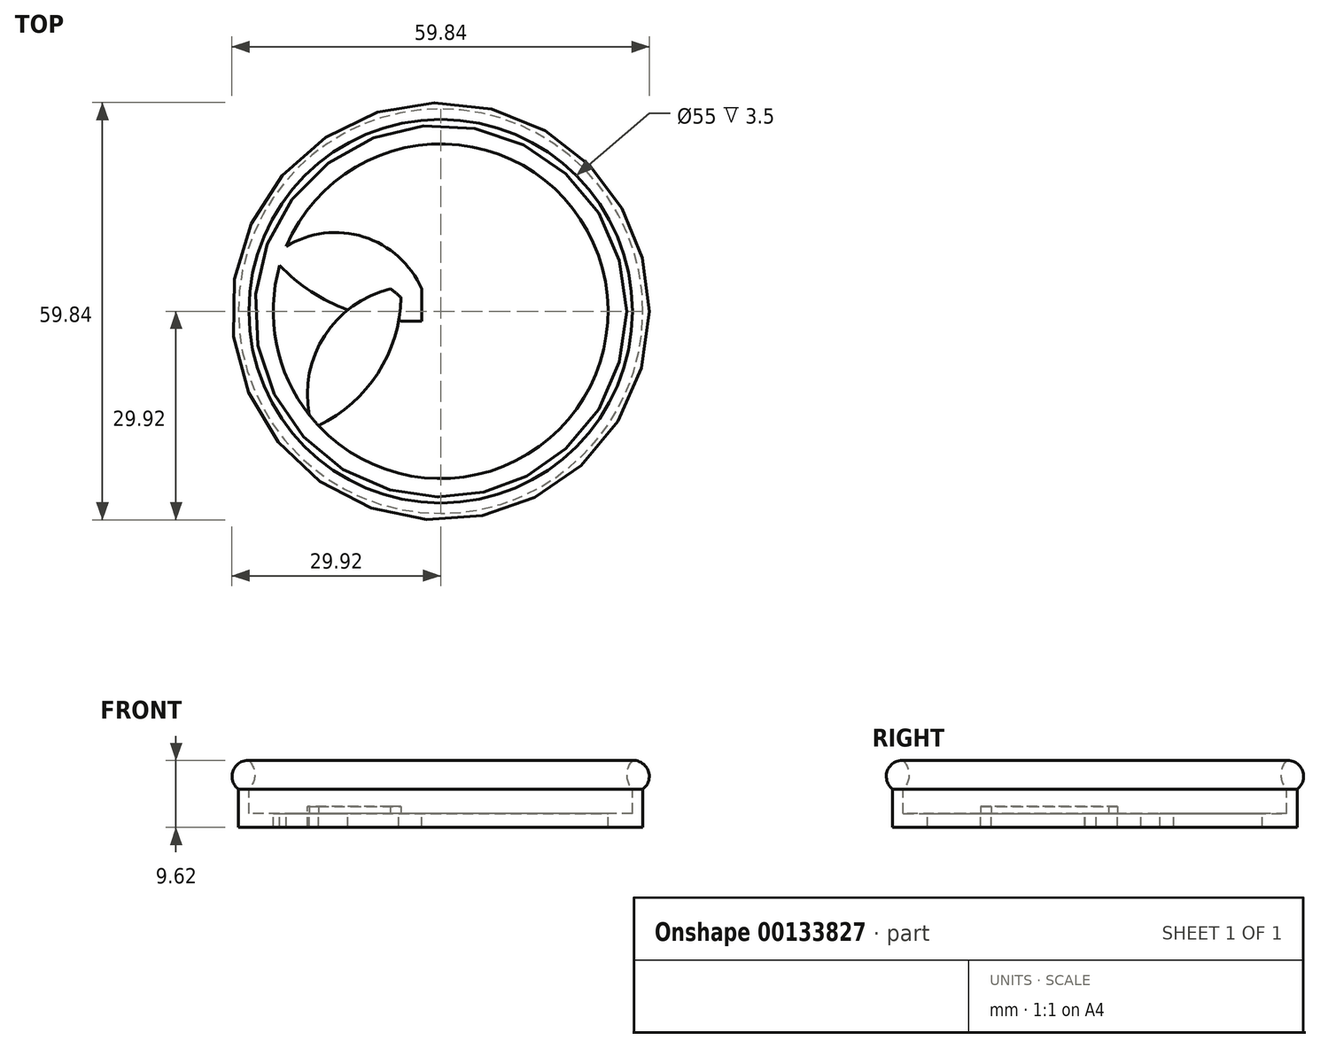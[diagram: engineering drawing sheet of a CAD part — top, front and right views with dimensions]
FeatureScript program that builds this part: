
annotation { "Feature Type Name" : "Feature", "Feature Type Description" : "" }
export const myFeature = defineFeature(function(context is Context, id is Id, definition is map)
    precondition{}
    {
        {
            var Q0;
            Q0=qCreatedBy(makeId("Front.planeOp"),FACE);
            var sketch = newSketch(context, id + "F0", { "sketchPlane" : qUnion([Q0])});
            skLineSegment(sketch, "E0", {"start": v(0, 25.71) * mm, "end": v(0, -20.29) * mm, "construction": true});
            skLineSegment(sketch, "E1", {"start": v(0, -20.29) * mm, "end": v(-42.81, -11.54) * mm, "construction": true});
            skLineSegment(sketch, "E2.0", {"start": v(-24, 25.71) * mm, "end": v(-24, -20.29) * mm, "construction": true});
            skLineSegment(sketch, "E3.0", {"start": v(-29, 25.71) * mm, "end": v(-29, -20.29) * mm, "construction": true});
            skLineSegment(sketch, "E4.0", {"start": v(-27.5, 25.71) * mm, "end": v(-27.5, -20.29) * mm, "construction": true});
            skLineSegment(sketch, "E5", {"start": v(-24, 0) * mm, "end": v(-29, 0) * mm});
            skLineSegment(sketch, "E6", {"start": v(-24, 0) * mm, "end": v(-24, 2) * mm});
            skLineSegment(sketch, "E7", {"start": v(-24, 2) * mm, "end": v(-27.5, 2) * mm});
            skLineSegment(sketch, "E8", {"start": v(-27.5, 2) * mm, "end": v(-27.5, 5.5) * mm});
            skLineSegment(sketch, "E9", {"start": v(-27.5, 5.5) * mm, "end": v(-29, 5.5) * mm});
            skLineSegment(sketch, "E10", {"start": v(-29, 5.5) * mm, "end": v(-29, 0) * mm});
            skArc(sketch, "E11", {"start": v(-27.5, 5.5) * mm, "mid": v(-26.66, 7.56) * mm, "end": v(-27.5, 9.62) * mm});
            skArc(sketch, "E12", {"start": v(-27.5, 9.62) * mm, "mid": v(-29.78, 8.11) * mm, "end": v(-29, 5.5) * mm});
            skSolve(sketch);
        }
        {
            var Q0;
            Q0=makeQuery(id+"F0.imprint","IMPRINT",FACE,{"disambiguationData":[TD([[makeQuery(id+"F0.imprint","IMPRINT",EDGE,{"derivedFrom":sQuery(id+"F0.wireOp",EDGE,"E5")}),-1.0]])]});
            var Q1;
            Q1=makeQuery(id+"F0.imprint","IMPRINT",FACE,{"disambiguationData":[TD([[makeQuery(id+"F0.imprint","IMPRINT",EDGE,{"derivedFrom":sQuery(id+"F0.wireOp",EDGE,"E9")}),-1.0]])]});
            var Q2;
            Q2=sQuery(id+"F0.wireOp",EDGE,"E0");
            revolve(context, id + "F1", {"entities" : qUnion([Q0, Q1]), "axis" : qUnion([Q2]), "revolveType" : RevolveType.FULL});
        }
        {
            var Q0;
            Q0=makeQuery(id+"F1.opRevolve","SWEPT_FACE",FACE,{"disambiguationData":[OSD([sQuery(id+"F0.wireOp",EDGE,"E7")])]});
            var sketch = newSketch(context, id + "F2", { "sketchPlane" : qUnion([Q0])});
            skCircle(sketch, "E13.0", {"center": v(0, 0) * mm, "radius": 24 * mm});
            skLineSegment(sketch, "E14", {"start": v(-2.72, 23.85) * mm, "end": v(-2.72, -23.85) * mm});
            skLineSegment(sketch, "E15", {"start": v(23.85, -2.68) * mm, "end": v(23.54, -2.01) * mm});
            skLineSegment(sketch, "E16", {"start": v(13, 20.18) * mm, "end": v(1.5, 23.95) * mm});
            skLineSegment(sketch, "E17", {"start": v(1.5, 19.86) * mm, "end": v(1.5, -17.1) * mm});
            skLineSegment(sketch, "E18", {"start": v(1.5, -17.1) * mm, "end": v(19.97, -1.22) * mm});
            skLineSegment(sketch, "E19", {"start": v(19.97, -1.22) * mm, "end": v(11.75, 17.98) * mm});
            skLineSegment(sketch, "E20", {"start": v(11.75, 17.98) * mm, "end": v(1.5, 19.86) * mm});
            skLineSegment(sketch, "E21", {"start": v(1.4, -23.96) * mm, "end": v(23.34, -5.58) * mm});
            skLineSegment(sketch, "E22", {"start": v(14.12, 19.4) * mm, "end": v(23.54, -2.01) * mm});
            skArc(sketch, "E23", {"start": v(-2.72, 3.2) * mm, "mid": v(-11.04, 10.67) * mm, "end": v(-22.13, 9.3) * mm});
            skArc(sketch, "E24", {"start": v(-2.72, -1.4) * mm, "mid": v(-11.69, 5.69) * mm, "end": v(-23.08, 6.57) * mm});
            skArc(sketch, "E25", {"start": v(-17.53, -16.4) * mm, "mid": v(-9, -8.9) * mm, "end": v(-5.67, 1.96) * mm});
            skArc(sketch, "E26", {"start": v(-7.2, 3.2) * mm, "mid": v(-16.63, -3.5) * mm, "end": v(-18.83, -14.88) * mm});
            skArc(sketch, "E27", {"start": v(-23.08, 6.57) * mm, "mid": v(-13.77, 0.36) * mm, "end": v(-2.72, -1.4) * mm});
            skSolve(sketch);
        }
        {
            var Q0;
            {var subQ0=sQuery(id+"F2.wireOp",EDGE,"E14");Q0=makeQuery(id+"F2.imprint","IMPRINT",FACE,{"disambiguationData":[TD([[makeQuery(id+"F2.imprint","IMPRINT",EDGE,{"derivedFrom":subQ0}),1.0]])]});}
            var Q1;
            {var subQ0=sQuery(id+"F2.wireOp",EDGE,"V51A80Wz-ZXtj-xEFj-0V65-WFEzXSAI5ttg");Q1=makeQuery(id+"F2.imprint","IMPRINT",FACE,{"disambiguationData":[TD([[makeQuery(id+"F2.imprint","IMPRINT",EDGE,{"derivedFrom":subQ0}),-1.0]])]});}
            var Q2;
            {var subQ5=sQuery(id+"F2.wireOp",EDGE,"E23");Q2=makeQuery(id+"F2.imprint","IMPRINT",FACE,{"disambiguationData":[TD([[makeQuery(id+"F2.imprint","IMPRINT",EDGE,{"derivedFrom":subQ5}),1.0]])]});}
            var Q3;
            {var subQ1=sQuery(id+"F2.wireOp",EDGE,"E24");var subQ3=sQuery(id+"F2.wireOp",EDGE,"E26");var subQ4=makeQuery(id+"F2.imprint","INTERSECT",VERTEX,{"derivedFrom":[subQ1,subQ3]});Q3=makeQuery(id+"F2.imprint","IMPRINT",FACE,{"disambiguationData":[TD([[makeQuery(id+"F2.imprint","IMPRINT",EDGE,{"disambiguationData":[TD([[subQ4,-1.0]])],"derivedFrom":subQ3}),-1.0]])]});}
            var Q4;
            {var subQ0=sQuery(id+"F2.wireOp",EDGE,"E25");var subQ1=sQuery(id+"F2.wireOp",EDGE,"E24");var subQ2=makeQuery(id+"F2.imprint","INTERSECT",VERTEX,{"derivedFrom":[subQ1,subQ0]});Q4=makeQuery(id+"F2.imprint","IMPRINT",FACE,{"disambiguationData":[TD([[makeQuery(id+"F2.imprint","IMPRINT",EDGE,{"disambiguationData":[TD([[subQ2,-1.0]])],"derivedFrom":subQ1}),1.0]])]});}
            var Q5;
            {var subQ0=sQuery(id+"F2.wireOp",EDGE,"E25");var subQ1=sQuery(id+"F2.wireOp",EDGE,"E13.0");var subQ2=makeQuery(id+"F2.imprint","INTERSECT",VERTEX,{"derivedFrom":[subQ1,subQ0]});Q5=makeQuery(id+"F2.imprint","IMPRINT",FACE,{"disambiguationData":[TD([[makeQuery(id+"F2.imprint","IMPRINT",EDGE,{"disambiguationData":[TD([[subQ2,1.0]])],"derivedFrom":subQ1}),1.0]])]});}
            var Q6;
            {var subQ1=sQuery(id+"F2.wireOp",EDGE,"E24");var subQ3=sQuery(id+"F2.wireOp",EDGE,"E25");var subQ4=makeQuery(id+"F2.imprint","INTERSECT",VERTEX,{"derivedFrom":[subQ1,subQ3]});Q6=makeQuery(id+"F2.imprint","IMPRINT",FACE,{"disambiguationData":[TD([[makeQuery(id+"F2.imprint","IMPRINT",EDGE,{"disambiguationData":[TD([[subQ4,1.0]])],"derivedFrom":subQ3}),-1.0]])]});}
            extrude(context, id + "F3", {"entities" : qUnion([Q0, Q1, Q2, Q3, Q4, Q5, Q6]), "operationType" : NewBodyOperationType.ADD, "oppositeDirection" : true, "depth" : 2 * mm});
        }
        {
            var Q0;
            {var subQ0=sQuery(id+"F2.wireOp",EDGE,"E25");var subQ1=sQuery(id+"F2.wireOp",EDGE,"E13.0");var subQ2=makeQuery(id+"F2.imprint","INTERSECT",VERTEX,{"derivedFrom":[subQ1,subQ0]});Q0=makeQuery(id+"F2.imprint","IMPRINT",FACE,{"disambiguationData":[TD([[makeQuery(id+"F2.imprint","IMPRINT",EDGE,{"disambiguationData":[TD([[subQ2,1.0]])],"derivedFrom":subQ1}),1.0]])]});}
            var Q1;
            {var subQ0=sQuery(id+"F2.wireOp",EDGE,"E25");var subQ1=sQuery(id+"F2.wireOp",EDGE,"E24");var subQ2=makeQuery(id+"F2.imprint","INTERSECT",VERTEX,{"derivedFrom":[subQ1,subQ0]});Q1=makeQuery(id+"F2.imprint","IMPRINT",FACE,{"disambiguationData":[TD([[makeQuery(id+"F2.imprint","IMPRINT",EDGE,{"disambiguationData":[TD([[subQ2,-1.0]])],"derivedFrom":subQ1}),1.0]])]});}
            extrude(context, id + "F4", {"entities" : qUnion([Q0, Q1]), "operationType" : NewBodyOperationType.ADD, "depth" : 1 * mm});
        }
    });
